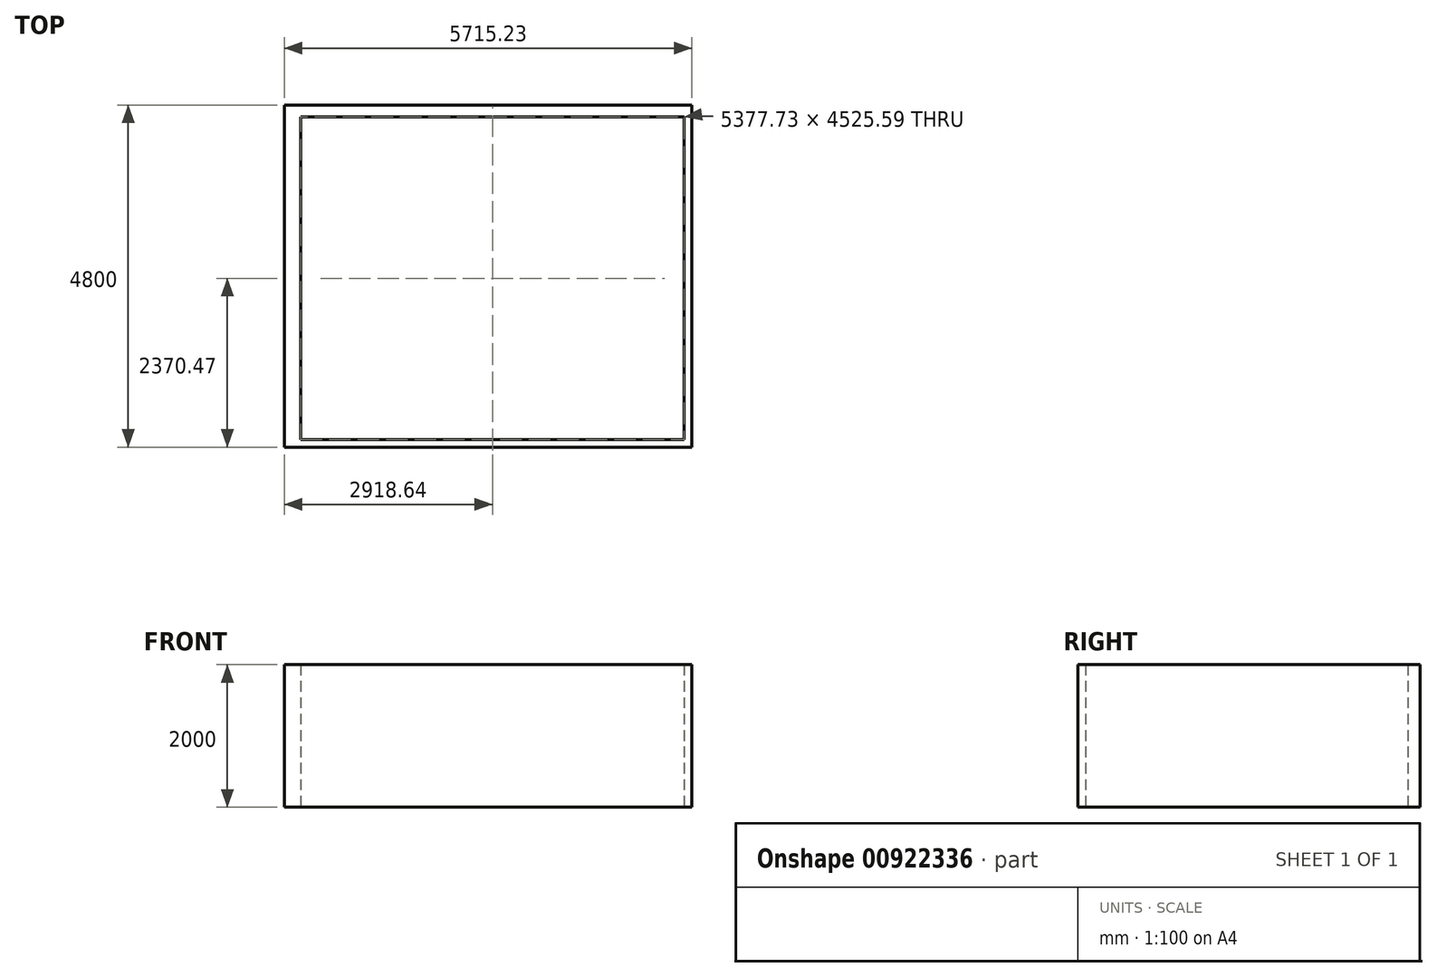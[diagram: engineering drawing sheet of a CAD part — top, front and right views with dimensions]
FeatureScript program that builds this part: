
annotation { "Feature Type Name" : "Feature", "Feature Type Description" : "" }
export const myFeature = defineFeature(function(context is Context, id is Id, definition is map)
    precondition{}
    {
        {
            var Q0;
            Q0=qCreatedBy(makeId("Top.planeOp"),FACE);
            var sketch = newSketch(context, id + "F0", { "sketchPlane" : qUnion([Q0])});
            skLineSegment(sketch, "E0.bottom", {"start": v(-2857.95, 2403.15) * mm, "end": v(2857.28, 2403.15) * mm});
            skLineSegment(sketch, "E0.top", {"start": v(-2857.95, -2396.85) * mm, "end": v(2857.28, -2396.85) * mm});
            skLineSegment(sketch, "E0.left", {"start": v(-2857.95, 2403.15) * mm, "end": v(-2857.95, -2396.85) * mm});
            skLineSegment(sketch, "E0.right", {"start": v(2857.28, 2403.15) * mm, "end": v(2857.28, -2396.85) * mm});
            skLineSegment(sketch, "E1.bottom", {"start": v(-2628.18, 2236.42) * mm, "end": v(2749.55, 2236.42) * mm});
            skLineSegment(sketch, "E1.top", {"start": v(-2628.18, -2289.17) * mm, "end": v(2749.55, -2289.17) * mm});
            skLineSegment(sketch, "E1.left", {"start": v(-2628.18, 2236.42) * mm, "end": v(-2628.18, -2289.17) * mm});
            skLineSegment(sketch, "E1.right", {"start": v(2749.55, 2236.42) * mm, "end": v(2749.55, -2289.17) * mm});
            skSolve(sketch);
        }
        {
            var Q0;
            Q0=makeQuery(id+"F0.imprint","IMPRINT",FACE,{"disambiguationData":[TD([[makeQuery(id+"F0.imprint","IMPRINT",EDGE,{"derivedFrom":sQuery(id+"F0.wireOp",EDGE,"E0.bottom")}),-1.0]])]});
            extrude(context, id + "F1", {"entities" : qUnion([Q0]), "depth" : 2000 * mm, "offsetDistance" : 25 * mm});
        }
    });
